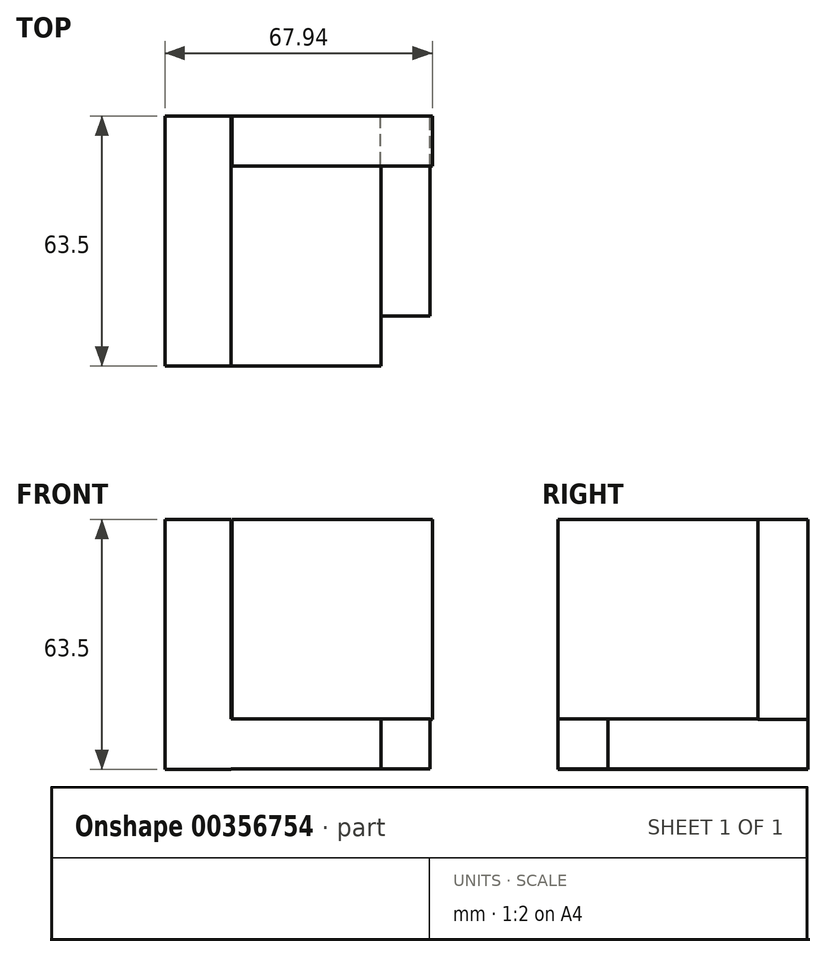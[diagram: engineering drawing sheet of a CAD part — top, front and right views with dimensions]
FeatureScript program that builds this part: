
annotation { "Feature Type Name" : "Feature", "Feature Type Description" : "" }
export const myFeature = defineFeature(function(context is Context, id is Id, definition is map)
    precondition{}
    {
        {
            var Q0;
            Q0=qCreatedBy(makeId("Front.planeOp"),FACE);
            var sketch = newSketch(context, id + "F0", { "sketchPlane" : qUnion([Q0])});
            skLineSegment(sketch, "E0.bottom", {"start": v(0, 0) * mm, "end": v(16.88, 0) * mm});
            skLineSegment(sketch, "E0.top", {"start": v(0, -63.5) * mm, "end": v(16.88, -63.5) * mm});
            skLineSegment(sketch, "E0.left", {"start": v(0, 0) * mm, "end": v(0, -63.5) * mm});
            skLineSegment(sketch, "E0.right", {"start": v(16.88, 0) * mm, "end": v(16.88, -63.5) * mm});
            skLineSegment(sketch, "E1.bottom", {"start": v(16.88, -50.65) * mm, "end": v(54.98, -50.65) * mm});
            skLineSegment(sketch, "E1.top", {"start": v(16.88, -63.35) * mm, "end": v(54.98, -63.35) * mm});
            skLineSegment(sketch, "E1.left", {"start": v(16.88, -50.65) * mm, "end": v(16.88, -63.35) * mm});
            skLineSegment(sketch, "E1.right", {"start": v(54.98, -50.65) * mm, "end": v(54.98, -63.35) * mm});
            skSolve(sketch);
        }
        {
            var Q0;
            Q0 = qSketchRegion(id + "F0", true);
            extrude(context, id + "F1", {"entities" : qUnion([Q0]), "depth" : 63.5 * mm});
        }
        {
            var Q0;
            Q0=qCreatedBy(makeId("Front.planeOp"),FACE);
            var sketch = newSketch(context, id + "F2", { "sketchPlane" : qUnion([Q0])});
            skLineSegment(sketch, "E2.bottom", {"start": v(55.6, -62.86) * mm, "end": v(66.39, -62.86) * mm});
            skLineSegment(sketch, "E2.top", {"start": v(55.6, -50.62) * mm, "end": v(66.39, -50.62) * mm});
            skLineSegment(sketch, "E2.left", {"start": v(55.6, -62.86) * mm, "end": v(55.6, -50.62) * mm});
            skLineSegment(sketch, "E2.right", {"start": v(66.39, -62.86) * mm, "end": v(66.39, -50.62) * mm});
            skSolve(sketch);
        }
        {
            var Q0;
            Q0 = qSketchRegion(id + "F2", true);
            var Q1;
            Q1=makeQuery(id+"F2.imprint","IMPRINT",FACE,{"disambiguationData":[TD([[makeQuery(id+"F2.imprint","IMPRINT",EDGE,{"derivedFrom":sQuery(id+"F2.wireOp",EDGE,"E2.bottom")}),1.0]])]});
            extrude(context, id + "F3", {"entities" : qUnion([Q0, Q1]), "depth" : 25.4 * mm});
        }
        {
            var Q0;
            Q0=makeQuery(id+"F3.opExtrude","SWEPT_BODY",BODY,{"disambiguationData":[OSD([sQuery(id+"F2.wireOp",EDGE,"E2.bottom"),sQuery(id+"F2.wireOp",EDGE,"E2.top"),sQuery(id+"F2.wireOp",EDGE,"E2.left"),sQuery(id+"F2.wireOp",EDGE,"E2.right")])]});
            deleteBodies(context, id + "F4", {"entities" : qUnion([Q0])});
        }
        {
            var Q0;
            Q0=qCreatedBy(makeId("Front.planeOp"),FACE);
            var sketch = newSketch(context, id + "F5", { "sketchPlane" : qUnion([Q0])});
            skLineSegment(sketch, "E3.bottom", {"start": v(54.64, -63.4) * mm, "end": v(67.34, -63.4) * mm});
            skLineSegment(sketch, "E3.top", {"start": v(54.64, -50.7) * mm, "end": v(67.34, -50.7) * mm});
            skLineSegment(sketch, "E3.left", {"start": v(54.64, -63.4) * mm, "end": v(54.64, -50.7) * mm});
            skLineSegment(sketch, "E3.right", {"start": v(67.34, -63.4) * mm, "end": v(67.34, -50.7) * mm});
            skSolve(sketch);
        }
        {
            var Q0;
            Q0 = qSketchRegion(id + "F5", true);
            extrude(context, id + "F6", {"entities" : qUnion([Q0]), "operationType" : NewBodyOperationType.ADD, "depth" : 50.8 * mm});
        }
        {
            var Q0;
            Q0=qCreatedBy(makeId("Front.planeOp"),FACE);
            var sketch = newSketch(context, id + "F7", { "sketchPlane" : qUnion([Q0])});
            skLineSegment(sketch, "E4.bottom", {"start": v(17.14, 0) * mm, "end": v(67.94, 0) * mm});
            skLineSegment(sketch, "E4.top", {"start": v(17.14, -50.8) * mm, "end": v(67.94, -50.8) * mm});
            skLineSegment(sketch, "E4.left", {"start": v(17.14, 0) * mm, "end": v(17.14, -50.8) * mm});
            skLineSegment(sketch, "E4.right", {"start": v(67.94, 0) * mm, "end": v(67.94, -50.8) * mm});
            skSolve(sketch);
        }
        {
            var Q0;
            Q0 = qSketchRegion(id + "F7", true);
            extrude(context, id + "F8", {"entities" : qUnion([Q0]), "operationType" : NewBodyOperationType.ADD, "depth" : 12.7 * mm});
        }
    });
